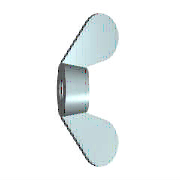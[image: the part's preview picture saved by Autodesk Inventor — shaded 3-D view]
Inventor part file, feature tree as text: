
AUTODESK INVENTOR PART (.ipt)
format: ipt  version: 2023 (Build 270158000, 158)  size: 168,960 bytes
history: native  units: mm (DEFAULTED — no unit token found)
features: sketch x2, other x2, extrude x1, mirror x1, hole x1, plane x1
ambient origin geometry x7: Origin, YZ Plane, XZ Plane, X Axis, Y Axis, Z Axis, Center Point
bodies: Solid1 (feature_tree)
feature tree (8):
  sketch  "Эскиз1"
  other  "Базовый элемент"
  extrude  "Крыло1"  Depth=11.0mm
  mirror  "Крыло2"
  hole  "Резьба"  [1 undecoded]
  other  "Work Axis1"
  plane  "Work Plane1"
  sketch  "Эскиз2"
note: 1 required parameter value undecoded (feature->parameter linkage not recoverable at this tier; creation-order binding heuristic only, values carry confidence <= 0.55)
